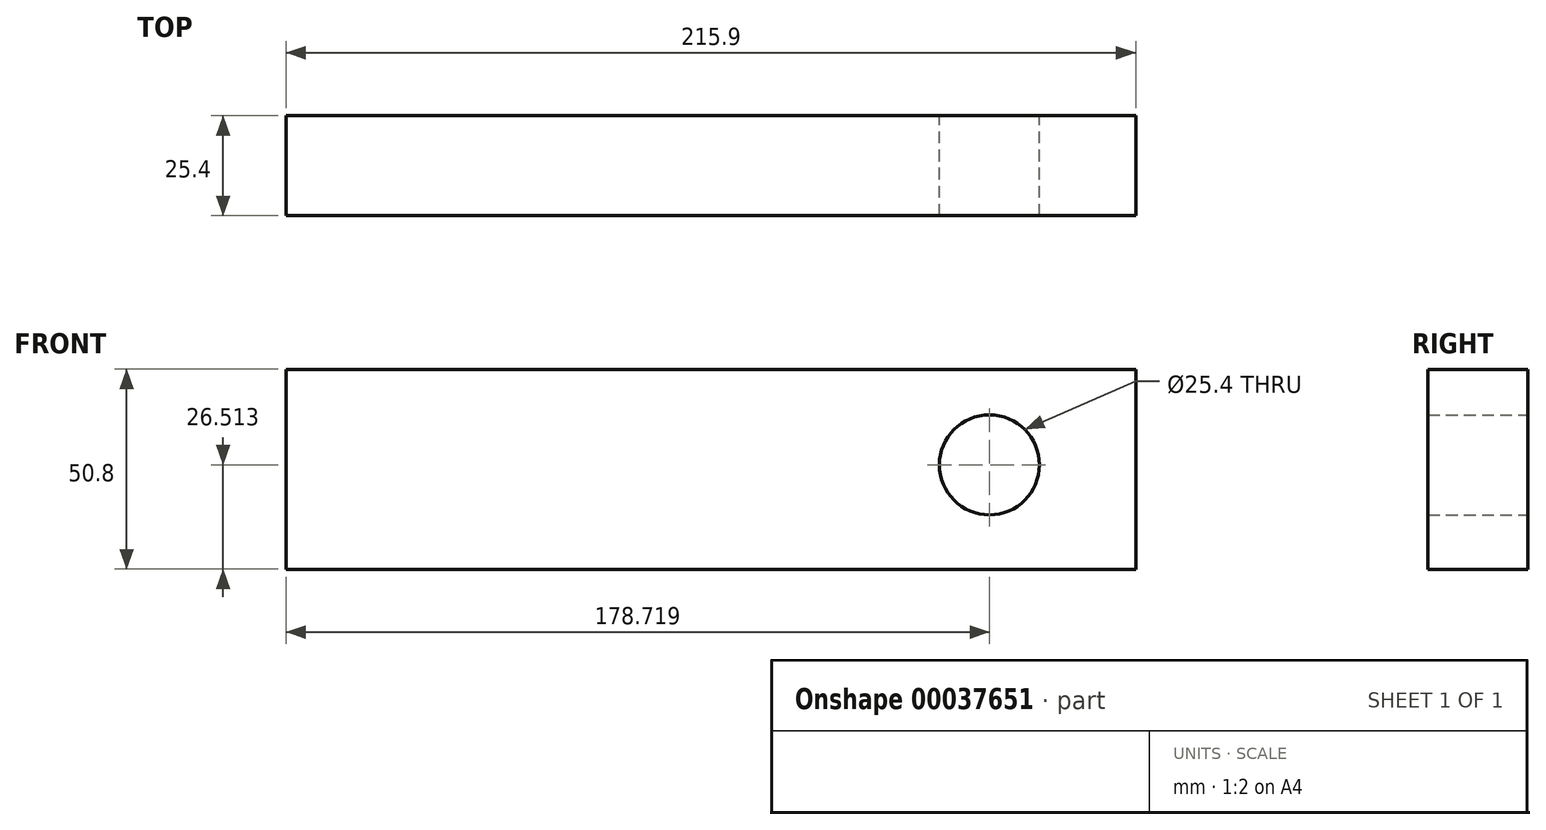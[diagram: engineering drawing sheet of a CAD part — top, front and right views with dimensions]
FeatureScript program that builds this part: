
annotation { "Feature Type Name" : "Feature", "Feature Type Description" : "" }
export const myFeature = defineFeature(function(context is Context, id is Id, definition is map)
    precondition{}
    {
        {
            var Q0;
            Q0=qCreatedBy(makeId("Front.planeOp"),FACE);
            var sketch = newSketch(context, id + "F0", { "sketchPlane" : qUnion([Q0])});
            skLineSegment(sketch, "E0.bottom", {"start": v(-104.56, -7.27) * mm, "end": v(111.34, -7.27) * mm});
            skLineSegment(sketch, "E0.top", {"start": v(-104.56, -58.07) * mm, "end": v(111.34, -58.07) * mm});
            skLineSegment(sketch, "E0.left", {"start": v(-104.56, -7.27) * mm, "end": v(-104.56, -58.07) * mm});
            skLineSegment(sketch, "E0.right", {"start": v(111.34, -7.27) * mm, "end": v(111.34, -58.07) * mm});
            skLineSegment(sketch, "E1", {"start": v(-104.56, -7.27) * mm, "end": v(3.39, -7.27) * mm});
            skLineSegment(sketch, "E2", {"start": v(111.34, -7.27) * mm, "end": v(111.34, -32.67) * mm});
            skCircle(sketch, "E3", {"center": v(74.16, -31.56) * mm, "radius": 12.7 * mm});
            skSolve(sketch);
        }
        {
            var Q0;
            Q0 = qSketchRegion(id + "F0", true);
            extrude(context, id + "F1", {"entities" : qUnion([Q0]), "depth" : 25.4 * mm});
        }
    });
